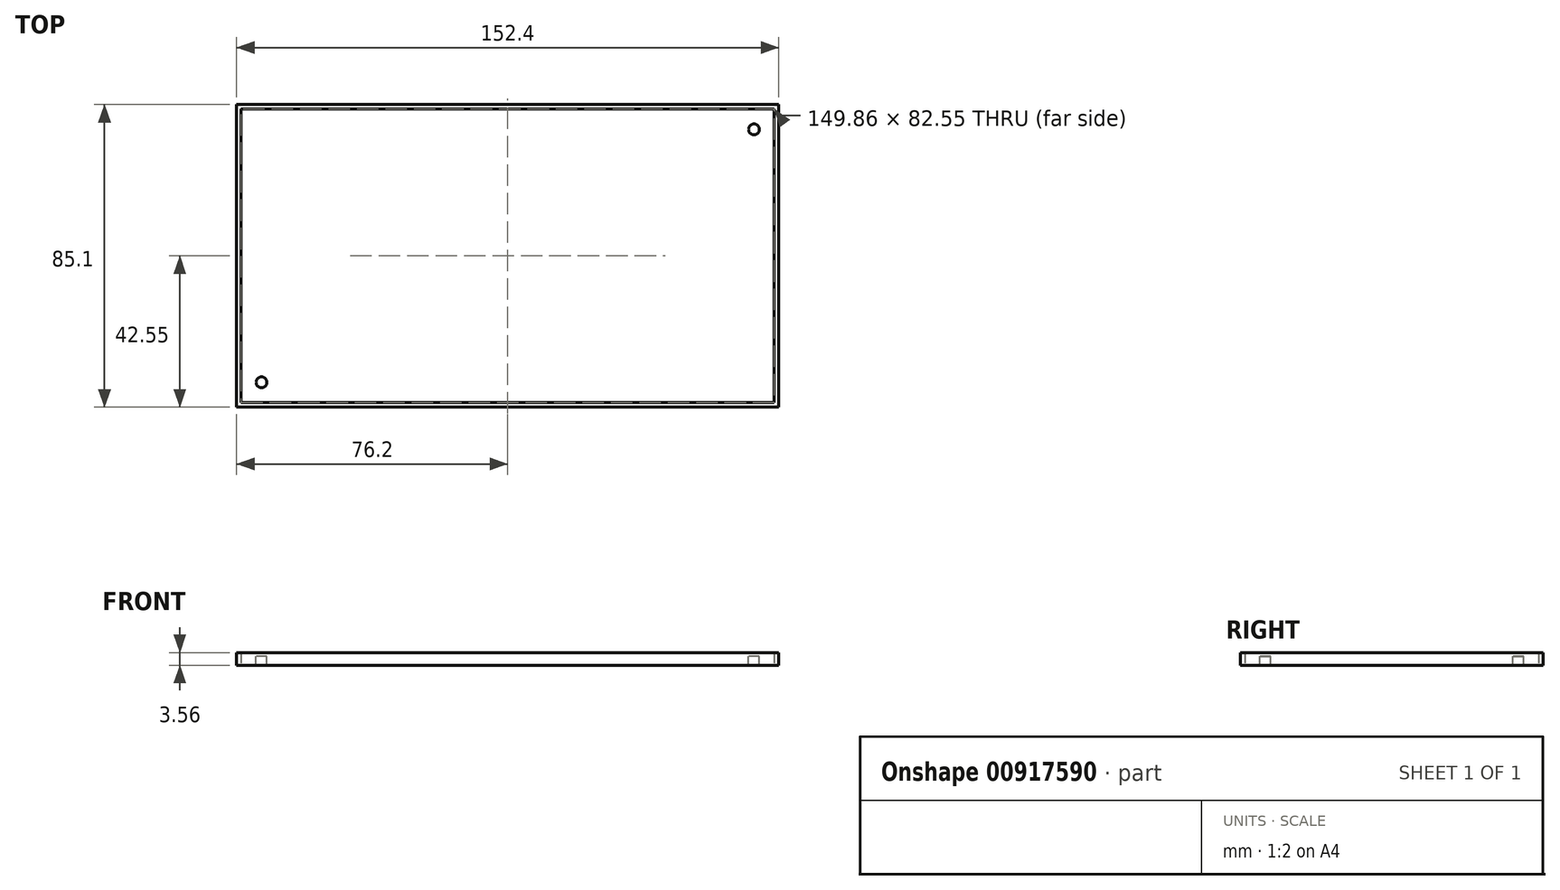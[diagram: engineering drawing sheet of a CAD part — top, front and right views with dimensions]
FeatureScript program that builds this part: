
annotation { "Feature Type Name" : "Feature", "Feature Type Description" : "" }
export const myFeature = defineFeature(function(context is Context, id is Id, definition is map)
    precondition{}
    {
        {
            var Q0;
            Q0=qCreatedBy(makeId("Top.planeOp"),FACE);
            var sketch = newSketch(context, id + "F0", { "sketchPlane" : qUnion([Q0])});
            skLineSegment(sketch, "E0.bottom", {"start": v(76.2, 42.55) * mm, "end": v(-76.2, 42.55) * mm});
            skLineSegment(sketch, "E0.top", {"start": v(76.2, -42.55) * mm, "end": v(-76.2, -42.55) * mm});
            skLineSegment(sketch, "E0.left", {"start": v(76.2, 42.55) * mm, "end": v(76.2, -42.55) * mm});
            skLineSegment(sketch, "E0.right", {"start": v(-76.2, 42.55) * mm, "end": v(-76.2, -42.55) * mm});
            skPoint(sketch, "E0.middle", {"position": v(0, 0) * mm});
            skSolve(sketch);
        }
        {
            var Q0;
            Q0=makeQuery(id+"F0.imprint","IMPRINT",FACE,{"disambiguationData":[TD([[makeQuery(id+"F0.imprint","IMPRINT",EDGE,{"derivedFrom":sQuery(id+"F0.wireOp",EDGE,"E0.bottom")}),1.0]])]});
            extrude(context, id + "F1", {"entities" : qUnion([Q0]), "depth" : 2.54 * mm, "offsetDistance" : 25.4 * mm});
        }
        {
            var Q0;
            Q0=makeQuery(id+"F1.opExtrude","CAP_FACE",FACE,{"disambiguationData":[OSD([sQuery(id+"F0.wireOp",EDGE,"E0.bottom"),sQuery(id+"F0.wireOp",EDGE,"E0.top"),sQuery(id+"F0.wireOp",EDGE,"E0.left"),sQuery(id+"F0.wireOp",EDGE,"E0.right")])],"isStart":false});
            var sketch = newSketch(context, id + "F2", { "sketchPlane" : qUnion([Q0])});
            skLineSegment(sketch, "E1.bottom", {"start": v(76.2, 42.55) * mm, "end": v(-76.2, 42.55) * mm});
            skLineSegment(sketch, "E1.top", {"start": v(76.2, -42.55) * mm, "end": v(-76.2, -42.55) * mm});
            skLineSegment(sketch, "E1.left", {"start": v(76.2, 42.55) * mm, "end": v(76.2, -42.55) * mm});
            skLineSegment(sketch, "E1.right", {"start": v(-76.2, 42.55) * mm, "end": v(-76.2, -42.55) * mm});
            skPoint(sketch, "E1.middle", {"position": v(0, 0) * mm});
            skLineSegment(sketch, "E2.bottom", {"start": v(74.93, 41.28) * mm, "end": v(-74.93, 41.28) * mm});
            skLineSegment(sketch, "E2.top", {"start": v(74.93, -41.28) * mm, "end": v(-74.93, -41.28) * mm});
            skLineSegment(sketch, "E2.left", {"start": v(74.93, 41.28) * mm, "end": v(74.93, -41.28) * mm});
            skLineSegment(sketch, "E2.right", {"start": v(-74.93, 41.28) * mm, "end": v(-74.93, -41.28) * mm});
            skSolve(sketch);
        }
        {
            var Q0;
            Q0=makeQuery(id+"F2.imprint","IMPRINT",FACE,{"disambiguationData":[TD([[makeQuery(id+"F2.imprint","IMPRINT",EDGE,{"derivedFrom":sQuery(id+"F2.wireOp",EDGE,"E1.bottom")}),1.0]])]});
            extrude(context, id + "F3", {"entities" : qUnion([Q0]), "operationType" : NewBodyOperationType.ADD, "depth" : 1.02 * mm, "offsetDistance" : 25.4 * mm});
        }
        {
            var Q0;
            Q0=makeQuery(id+"F1.opExtrude","CAP_FACE",FACE,{"disambiguationData":[OSD([sQuery(id+"F0.wireOp",EDGE,"E0.bottom"),sQuery(id+"F0.wireOp",EDGE,"E0.top"),sQuery(id+"F0.wireOp",EDGE,"E0.left"),sQuery(id+"F0.wireOp",EDGE,"E0.right")])],"isStart":false});
            var sketch = newSketch(context, id + "F4", { "sketchPlane" : qUnion([Q0])});
            skLineSegment(sketch, "E3", {"start": v(-74.93, 41.28) * mm, "end": v(-74.93, 40) * mm, "construction": true});
            skLineSegment(sketch, "E4", {"start": v(-74.93, 40) * mm, "end": v(-63.5, 40) * mm, "construction": true});
            skLineSegment(sketch, "E5", {"start": v(-63.5, 40) * mm, "end": v(-69.22, 40) * mm, "construction": true});
            skLineSegment(sketch, "E6", {"start": v(-69.22, 40) * mm, "end": v(-69.22, 31.12) * mm, "construction": true});
            skCircle(sketch, "E7", {"center": v(-69.22, 35.56) * mm, "radius": 1.52 * mm});
            skCircle(sketch, "E8.MirrorC", {"center": v(69.22, 35.56) * mm, "radius": 1.52 * mm});
            skCircle(sketch, "E9.MirrorC", {"center": v(-69.22, -35.56) * mm, "radius": 1.52 * mm});
            skCircle(sketch, "E10.MirrorC", {"center": v(69.22, -35.56) * mm, "radius": 1.52 * mm});
            skSolve(sketch);
        }
        {
            var Q0;
            Q0=makeQuery(id+"F4.imprint","IMPRINT",FACE,{"disambiguationData":[TD([[makeQuery(id+"F4.imprint","IMPRINT",EDGE,{"derivedFrom":sQuery(id+"F4.wireOp",EDGE,"E8.MirrorC")}),-1.0]])]});
            var Q1;
            Q1=makeQuery(id+"F4.imprint","IMPRINT",FACE,{"disambiguationData":[TD([[makeQuery(id+"F4.imprint","IMPRINT",EDGE,{"derivedFrom":sQuery(id+"F4.wireOp",EDGE,"E10.MirrorC")}),1.0]])]});
            var Q2;
            Q2=makeQuery(id+"F4.imprint","IMPRINT",FACE,{"disambiguationData":[TD([[makeQuery(id+"F4.imprint","IMPRINT",EDGE,{"derivedFrom":sQuery(id+"F4.wireOp",EDGE,"E7")}),1.0]])]});
            var Q3;
            Q3=makeQuery(id+"F4.imprint","IMPRINT",FACE,{"disambiguationData":[TD([[makeQuery(id+"F4.imprint","IMPRINT",EDGE,{"derivedFrom":sQuery(id+"F4.wireOp",EDGE,"E9.MirrorC")}),-1.0]])]});
            extrude(context, id + "F5", {"entities" : qUnion([Q0, Q1, Q2, Q3]), "operationType" : NewBodyOperationType.REMOVE, "oppositeDirection" : true, "depth" : 25.4 * mm, "offsetDistance" : 25.4 * mm});
        }
    });
